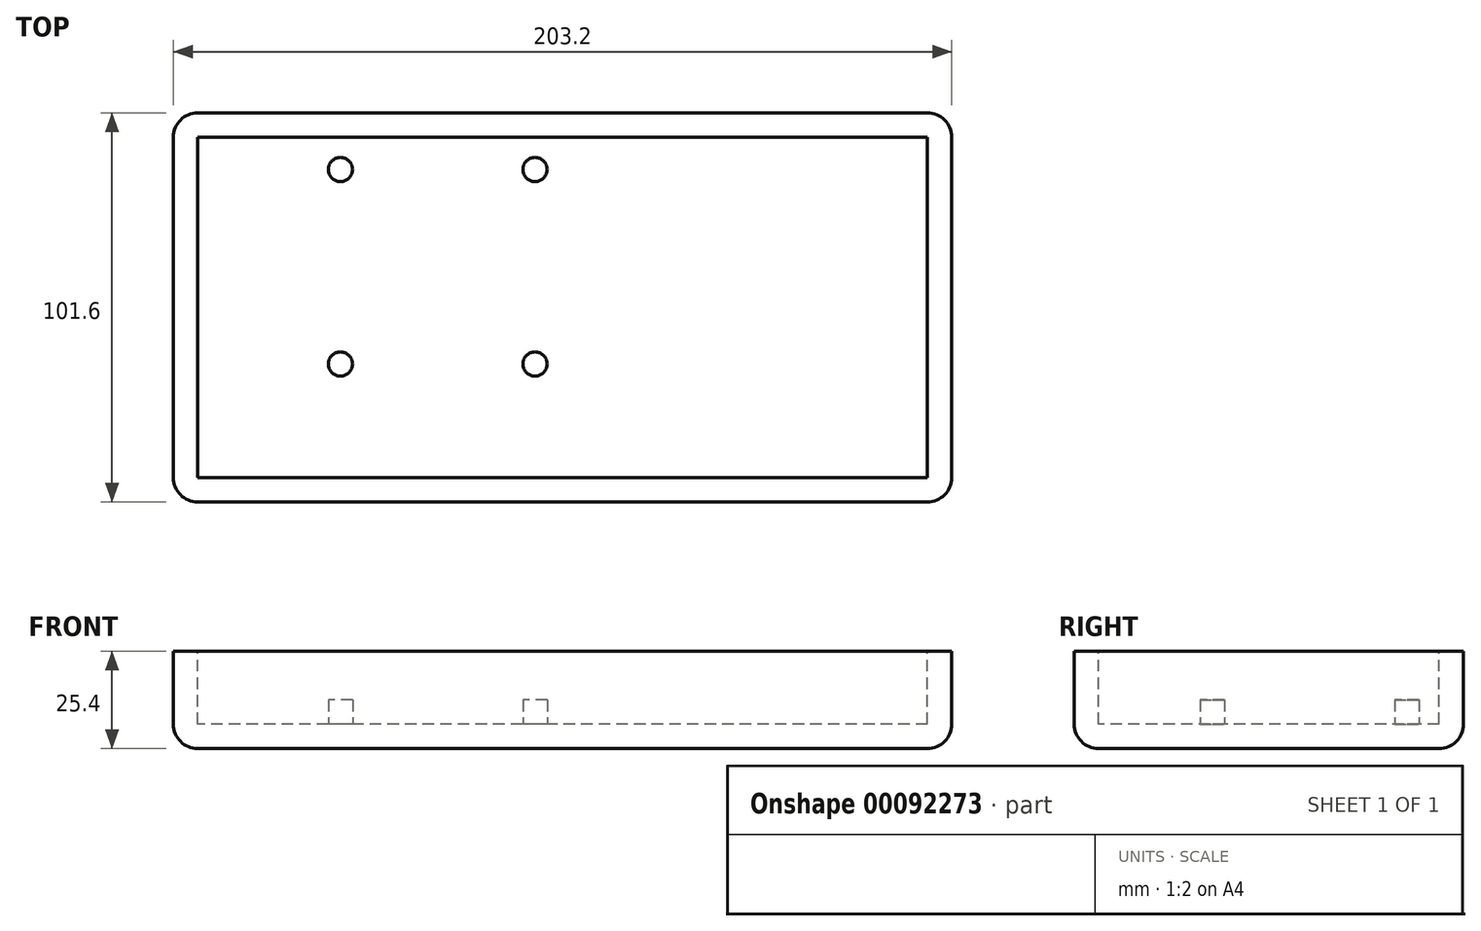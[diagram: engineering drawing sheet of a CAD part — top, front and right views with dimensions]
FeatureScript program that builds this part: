
annotation { "Feature Type Name" : "Feature", "Feature Type Description" : "" }
export const myFeature = defineFeature(function(context is Context, id is Id, definition is map)
    precondition{}
    {
        {
            var Q0;
            Q0=qCreatedBy(makeId("Top.planeOp"),FACE);
            var sketch = newSketch(context, id + "F0", { "sketchPlane" : qUnion([Q0])});
            skLineSegment(sketch, "E0.bottom", {"start": v(0, 0) * mm, "end": v(203.2, 0) * mm});
            skLineSegment(sketch, "E0.top", {"start": v(0, 101.6) * mm, "end": v(203.2, 101.6) * mm});
            skLineSegment(sketch, "E0.left", {"start": v(0, 0) * mm, "end": v(0, 101.6) * mm});
            skLineSegment(sketch, "E0.right", {"start": v(203.2, 0) * mm, "end": v(203.2, 101.6) * mm});
            skSolve(sketch);
        }
        {
            var Q0;
            Q0 = qSketchRegion(id + "F0", true);
            extrude(context, id + "F1", {"entities" : qUnion([Q0]), "depth" : 25.4 * mm});
        }
        {
            var Q0;
            Q0=makeQuery(id+"F1.opExtrude","SWEPT_EDGE",EDGE,{"disambiguationData":[OSD([sQuery(id+"F0.wireOp",EDGE,"E0.bottom"),sQuery(id+"F0.wireOp",EDGE,"E0.left")])]});
            var Q1;
            Q1=makeQuery(id+"F1.opExtrude","SWEPT_EDGE",EDGE,{"disambiguationData":[OSD([sQuery(id+"F0.wireOp",EDGE,"E0.bottom"),sQuery(id+"F0.wireOp",EDGE,"E0.right")])]});
            var Q2;
            Q2=makeQuery(id+"F1.opExtrude","SWEPT_EDGE",EDGE,{"disambiguationData":[OSD([sQuery(id+"F0.wireOp",EDGE,"E0.top"),sQuery(id+"F0.wireOp",EDGE,"E0.left")])]});
            var Q3;
            Q3=makeQuery(id+"F1.opExtrude","SWEPT_EDGE",EDGE,{"disambiguationData":[OSD([sQuery(id+"F0.wireOp",EDGE,"E0.top"),sQuery(id+"F0.wireOp",EDGE,"E0.right")])]});
            var Q4;
            Q4=makeQuery(id+"F1.opExtrude","CAP_EDGE",EDGE,{"disambiguationData":[OSD([sQuery(id+"F0.wireOp",EDGE,"E0.top")])],"isStart":true});
            var Q5;
            Q5=makeQuery(id+"F1.opExtrude","CAP_EDGE",EDGE,{"disambiguationData":[OSD([sQuery(id+"F0.wireOp",EDGE,"E0.left")])],"isStart":true});
            var Q6;
            Q6=makeQuery(id+"F1.opExtrude","CAP_EDGE",EDGE,{"disambiguationData":[OSD([sQuery(id+"F0.wireOp",EDGE,"E0.bottom")])],"isStart":true});
            var Q7;
            Q7=makeQuery(id+"F1.opExtrude","CAP_EDGE",EDGE,{"disambiguationData":[OSD([sQuery(id+"F0.wireOp",EDGE,"E0.right")])],"isStart":true});
            fillet(context, id + "F2", {"entities" : qUnion([Q0, Q1, Q2, Q3, Q4, Q5, Q6, Q7]), "radius" : 6.35 * mm, "tangentPropagation" : true, "allowEdgeOverflow" : false});
        }
        {
            var Q0;
            Q0=makeQuery(id+"F1.opExtrude","CAP_FACE",FACE,{"disambiguationData":[OSD([sQuery(id+"F0.wireOp",EDGE,"E0.bottom"),sQuery(id+"F0.wireOp",EDGE,"E0.top"),sQuery(id+"F0.wireOp",EDGE,"E0.left"),sQuery(id+"F0.wireOp",EDGE,"E0.right")])],"isStart":false});
            shell(context, id + "F3", {"entities" : qUnion([Q0]), "thickness" : 6.35 * mm});
        }
        {
            var Q0;
            Q0=makeQuery(id+"F3.opShell","OFFSET_FACE",FACE,{"disambiguationData":[OSD([sQuery(id+"F0.wireOp",EDGE,"E0.bottom"),sQuery(id+"F0.wireOp",EDGE,"E0.top"),sQuery(id+"F0.wireOp",EDGE,"E0.left"),sQuery(id+"F0.wireOp",EDGE,"E0.right")])]});
            var sketch = newSketch(context, id + "F4", { "sketchPlane" : qUnion([Q0])});
            skCircle(sketch, "E1", {"center": v(43.6, 86.82) * mm, "radius": 3.18 * mm});
            skCircle(sketch, "E2", {"center": v(43.6, 36.02) * mm, "radius": 3.18 * mm});
            skCircle(sketch, "E3", {"center": v(94.4, 36.02) * mm, "radius": 3.18 * mm});
            skCircle(sketch, "E4", {"center": v(94.4, 86.82) * mm, "radius": 3.18 * mm});
            skLineSegment(sketch, "E5.bottom", {"start": v(43.6, 86.82) * mm, "end": v(94.4, 86.82) * mm});
            skLineSegment(sketch, "E5.top", {"start": v(43.6, 36.02) * mm, "end": v(94.4, 36.02) * mm});
            skLineSegment(sketch, "E5.left", {"start": v(43.6, 86.82) * mm, "end": v(43.6, 36.02) * mm});
            skLineSegment(sketch, "E5.right", {"start": v(94.4, 86.82) * mm, "end": v(94.4, 36.02) * mm});
            skSolve(sketch);
        }
        {
            var Q0;
            {var subQ0=sQuery(id+"F4.wireOp",EDGE,"E5.bottom");var subQ1=sQuery(id+"F4.wireOp",EDGE,"E1");var subQ2=makeQuery(id+"F4.imprint","INTERSECT",VERTEX,{"derivedFrom":[subQ1,subQ0]});Q0=makeQuery(id+"F4.imprint","IMPRINT",FACE,{"disambiguationData":[TD([[makeQuery(id+"F4.imprint","IMPRINT",EDGE,{"disambiguationData":[TD([[subQ2,-1.0]])],"derivedFrom":subQ1}),1.0]])]});}
            var Q1;
            {var subQ0=sQuery(id+"F4.wireOp",EDGE,"E5.bottom");var subQ1=sQuery(id+"F4.wireOp",EDGE,"E1");var subQ2=makeQuery(id+"F4.imprint","INTERSECT",VERTEX,{"derivedFrom":[subQ1,subQ0]});Q1=makeQuery(id+"F4.imprint","IMPRINT",FACE,{"disambiguationData":[TD([[makeQuery(id+"F4.imprint","IMPRINT",EDGE,{"disambiguationData":[TD([[subQ2,1.0]])],"derivedFrom":subQ1}),1.0]])]});}
            var Q2;
            {var subQ0=sQuery(id+"F4.wireOp",EDGE,"E5.bottom");var subQ1=sQuery(id+"F4.wireOp",EDGE,"E4");var subQ2=makeQuery(id+"F4.imprint","INTERSECT",VERTEX,{"derivedFrom":[subQ1,subQ0]});Q2=makeQuery(id+"F4.imprint","IMPRINT",FACE,{"disambiguationData":[TD([[makeQuery(id+"F4.imprint","IMPRINT",EDGE,{"disambiguationData":[TD([[subQ2,1.0]])],"derivedFrom":subQ1}),1.0]])]});}
            var Q3;
            {var subQ0=sQuery(id+"F4.wireOp",EDGE,"E5.bottom");var subQ1=sQuery(id+"F4.wireOp",EDGE,"E4");var subQ2=makeQuery(id+"F4.imprint","INTERSECT",VERTEX,{"derivedFrom":[subQ1,subQ0]});Q3=makeQuery(id+"F4.imprint","IMPRINT",FACE,{"disambiguationData":[TD([[makeQuery(id+"F4.imprint","IMPRINT",EDGE,{"disambiguationData":[TD([[subQ2,-1.0]])],"derivedFrom":subQ1}),1.0]])]});}
            var Q4;
            {var subQ0=sQuery(id+"F4.wireOp",EDGE,"E5.top");var subQ1=sQuery(id+"F4.wireOp",EDGE,"E3");var subQ2=makeQuery(id+"F4.imprint","INTERSECT",VERTEX,{"derivedFrom":[subQ1,subQ0]});Q4=makeQuery(id+"F4.imprint","IMPRINT",FACE,{"disambiguationData":[TD([[makeQuery(id+"F4.imprint","IMPRINT",EDGE,{"disambiguationData":[TD([[subQ2,1.0]])],"derivedFrom":subQ1}),1.0]])]});}
            var Q5;
            {var subQ0=sQuery(id+"F4.wireOp",EDGE,"E5.top");var subQ1=sQuery(id+"F4.wireOp",EDGE,"E2");var subQ2=makeQuery(id+"F4.imprint","INTERSECT",VERTEX,{"derivedFrom":[subQ1,subQ0]});Q5=makeQuery(id+"F4.imprint","IMPRINT",FACE,{"disambiguationData":[TD([[makeQuery(id+"F4.imprint","IMPRINT",EDGE,{"disambiguationData":[TD([[subQ2,-1.0]])],"derivedFrom":subQ1}),1.0]])]});}
            var Q6;
            {var subQ0=sQuery(id+"F4.wireOp",EDGE,"E5.top");var subQ1=sQuery(id+"F4.wireOp",EDGE,"E2");var subQ2=makeQuery(id+"F4.imprint","INTERSECT",VERTEX,{"derivedFrom":[subQ1,subQ0]});Q6=makeQuery(id+"F4.imprint","IMPRINT",FACE,{"disambiguationData":[TD([[makeQuery(id+"F4.imprint","IMPRINT",EDGE,{"disambiguationData":[TD([[subQ2,1.0]])],"derivedFrom":subQ1}),1.0]])]});}
            var Q7;
            {var subQ0=sQuery(id+"F4.wireOp",EDGE,"E5.top");var subQ1=sQuery(id+"F4.wireOp",EDGE,"E3");var subQ2=makeQuery(id+"F4.imprint","INTERSECT",VERTEX,{"derivedFrom":[subQ1,subQ0]});Q7=makeQuery(id+"F4.imprint","IMPRINT",FACE,{"disambiguationData":[TD([[makeQuery(id+"F4.imprint","IMPRINT",EDGE,{"disambiguationData":[TD([[subQ2,-1.0]])],"derivedFrom":subQ1}),1.0]])]});}
            extrude(context, id + "F5", {"entities" : qUnion([Q0, Q1, Q2, Q3, Q4, Q5, Q6, Q7]), "operationType" : NewBodyOperationType.ADD, "depth" : 6.35 * mm});
        }
    });
